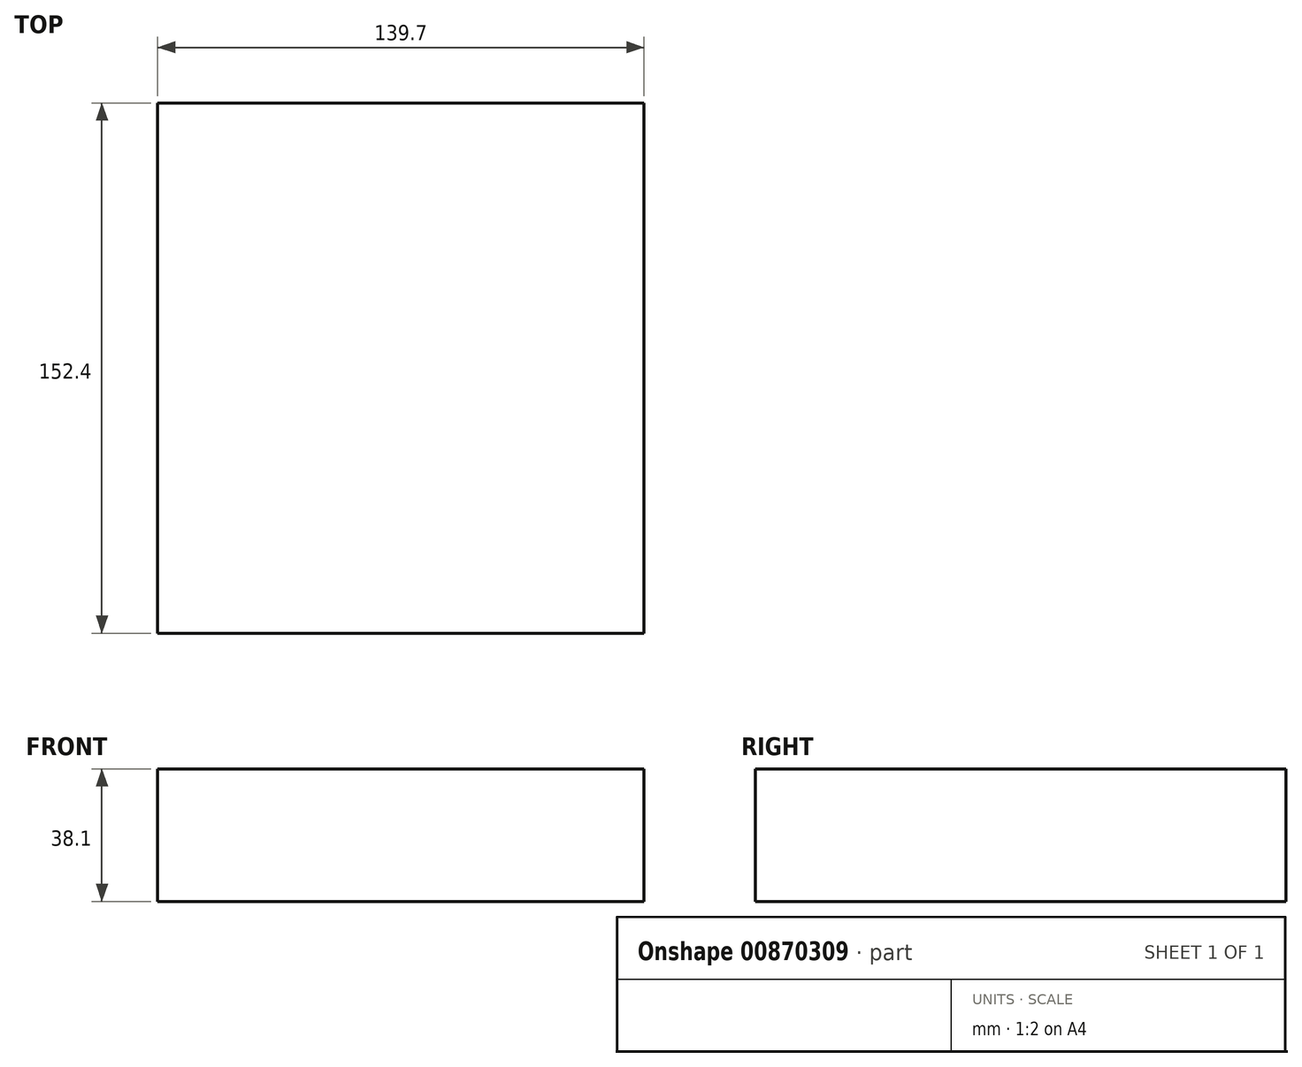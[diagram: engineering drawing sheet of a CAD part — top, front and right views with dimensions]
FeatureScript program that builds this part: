
annotation { "Feature Type Name" : "Feature", "Feature Type Description" : "" }
export const myFeature = defineFeature(function(context is Context, id is Id, definition is map)
    precondition{}
    {
        {
            var Q0;
            Q0=qCreatedBy(makeId("Front.planeOp"),FACE);
            var sketch = newSketch(context, id + "F0", { "sketchPlane" : qUnion([Q0])});
            skLineSegment(sketch, "E0.bottom", {"start": v(0, 0) * mm, "end": v(139.7, 0) * mm});
            skLineSegment(sketch, "E0.top", {"start": v(0, 38.1) * mm, "end": v(139.7, 38.1) * mm});
            skLineSegment(sketch, "E0.left", {"start": v(0, 0) * mm, "end": v(0, 38.1) * mm});
            skLineSegment(sketch, "E0.right", {"start": v(139.7, 0) * mm, "end": v(139.7, 38.1) * mm});
            skSolve(sketch);
        }
        {
            var Q0;
            Q0 = qSketchRegion(id + "F0", true);
            extrude(context, id + "F1", {"entities" : qUnion([Q0]), "depth" : 152.4 * mm, "offsetDistance" : 25.4 * mm});
        }
    });
